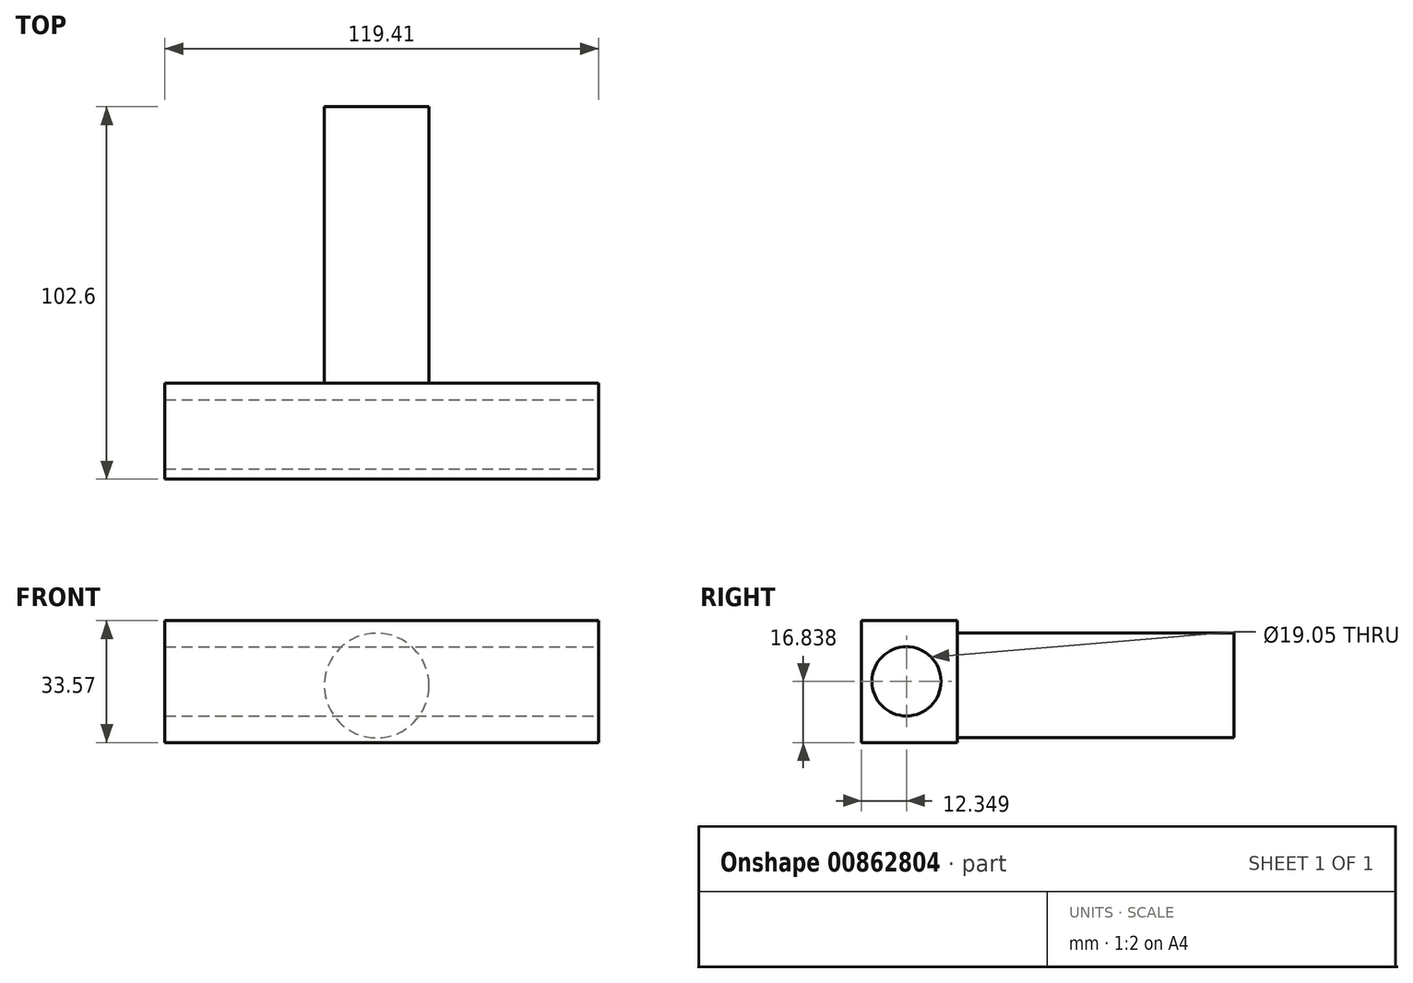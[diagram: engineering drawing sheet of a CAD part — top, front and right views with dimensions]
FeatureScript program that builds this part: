
annotation { "Feature Type Name" : "Feature", "Feature Type Description" : "" }
export const myFeature = defineFeature(function(context is Context, id is Id, definition is map)
    precondition{}
    {
        {
            var Q0;
            Q0=qCreatedBy(makeId("Front.planeOp"),FACE);
            var sketch = newSketch(context, id + "F0", { "sketchPlane" : qUnion([Q0])});
            skLineSegment(sketch, "E0.bottom", {"start": v(-58.32, -20.35) * mm, "end": v(61.1, -20.35) * mm});
            skLineSegment(sketch, "E0.top", {"start": v(-58.32, 13.22) * mm, "end": v(61.1, 13.22) * mm});
            skLineSegment(sketch, "E0.left", {"start": v(-58.32, -20.35) * mm, "end": v(-58.32, 13.22) * mm});
            skLineSegment(sketch, "E0.right", {"start": v(61.1, -20.35) * mm, "end": v(61.1, 13.22) * mm});
            skSolve(sketch);
        }
        {
            var Q0;
            Q0=makeQuery(id+"F0.imprint","IMPRINT",FACE,{"disambiguationData":[TD([[makeQuery(id+"F0.imprint","IMPRINT",EDGE,{"derivedFrom":sQuery(id+"F0.wireOp",EDGE,"E0.bottom")}),1.0]])]});
            extrude(context, id + "F1", {"entities" : qUnion([Q0]), "depth" : 1 * mm, "offsetDistance" : 25.4 * mm});
        }
        {
            var Q0;
            Q0=makeQuery(id+"F1.opExtrude","CAP_FACE",FACE,{"disambiguationData":[OSD([sQuery(id+"F0.wireOp",EDGE,"E0.bottom"),sQuery(id+"F0.wireOp",EDGE,"E0.top"),sQuery(id+"F0.wireOp",EDGE,"E0.left"),sQuery(id+"F0.wireOp",EDGE,"E0.right")])],"isStart":false});
            extrude(context, id + "F2", {"entities" : qUnion([Q0]), "operationType" : NewBodyOperationType.ADD, "depth" : 25.4 * mm, "offsetDistance" : 25.4 * mm});
        }
        {
            var Q0;
            {var subQ0=sQuery(id+"F0.wireOp",EDGE,"E0.right");Q0=makeQuery(id+"F2.boolean.opBoolean","MERGE",FACE,{"derivedFrom":[makeQuery(id+"F1.opExtrude","SWEPT_FACE",FACE,{"disambiguationData":[OSD([subQ0])]}),makeQuery(id+"F2.opExtrude","SWEPT_FACE",FACE,{"disambiguationData":[OSD([subQ0])]})]});}
            var sketch = newSketch(context, id + "F3", { "sketchPlane" : qUnion([Q0])});
            skCircle(sketch, "E1", {"center": v(-14.05, -3.51) * mm, "radius": 8.96 * mm});
            skSolve(sketch);
        }
        {
            var Q0;
            Q0=sQuery(id+"F3.wireOp",VERTEX,"E1.center");
            var Q1;
            Q1=makeQuery(id+"F1.opExtrude","SWEPT_BODY",BODY,{"disambiguationData":[OSD([sQuery(id+"F0.wireOp",EDGE,"E0.bottom"),sQuery(id+"F0.wireOp",EDGE,"E0.top"),sQuery(id+"F0.wireOp",EDGE,"E0.left"),sQuery(id+"F0.wireOp",EDGE,"E0.right")])]});
            hole(context, id + "F4", {"style" : HoleStyle.SIMPLE, "endStyle" : HoleEndStyle.THROUGH, "holeDiameter" : 19.05 * mm, "majorDiameter" : 6.35 * mm, "isTappedThrough" : true, "tappedDepth" : 12.7 * mm, "tapClearance" : 3, "locations" : qUnion([Q0]), "scope" : qUnion([Q1])});
        }
        {
            var Q0;
            Q0=makeQuery(id+"F1.opExtrude","CAP_FACE",FACE,{"disambiguationData":[OSD([sQuery(id+"F0.wireOp",EDGE,"E0.bottom"),sQuery(id+"F0.wireOp",EDGE,"E0.top"),sQuery(id+"F0.wireOp",EDGE,"E0.left"),sQuery(id+"F0.wireOp",EDGE,"E0.right")])],"isStart":true});
            var sketch = newSketch(context, id + "F5", { "sketchPlane" : qUnion([Q0])});
            skCircle(sketch, "E2", {"center": v(0, -4.65) * mm, "radius": 14.42 * mm});
            skSolve(sketch);
        }
        {
            var Q0;
            Q0=makeQuery(id+"F5.imprint","IMPRINT",FACE,{"disambiguationData":[TD([[makeQuery(id+"F5.imprint","IMPRINT",EDGE,{"derivedFrom":sQuery(id+"F5.wireOp",EDGE,"E2")}),1.0]])]});
            extrude(context, id + "F6", {"entities" : qUnion([Q0]), "operationType" : NewBodyOperationType.ADD, "depth" : 76.2 * mm, "offsetDistance" : 25.4 * mm});
        }
    });
